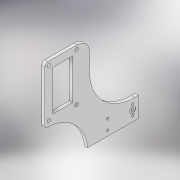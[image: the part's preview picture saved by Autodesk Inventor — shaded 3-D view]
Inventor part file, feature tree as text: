
AUTODESK INVENTOR PART (.ipt)
format: ipt  version: 2019 (Build 230136000, 136)  size: 181,248 bytes
history: native  units: mm
features: sketch x5, hole x4, extrude x1, other x1
ambient origin geometry x8: Origin, YZ Plane, XZ Plane, XY Plane, X Axis, Y Axis, Z Axis, Center Point
bodies: Solid1 (feature_tree)
feature tree (11):
  hole  "Hole1"  [1 undecoded]
  hole  "Hole2"  [1 undecoded]
  hole  "Hole3"  [1 undecoded]
  extrude  "Extrusion1"  [1 undecoded]
  hole  "Hole4"  [1 undecoded]
  sketch  "Sketch1"  dims[d0=6.756mm d1=6.0mm d2=12.878mm d3=2.0mm d4=14.3mm d5=78.0mm d6=20.594885mm]
  sketch  "Sketch2"  dims[d7=4.496mm d8=6.0mm d9=8.433mm d10=2.0mm d11=14.3mm d12=78.0mm d13=20.594885mm]
  sketch  "Sketch3"  dims[d14=4.496mm d15=6.0mm d16=8.433mm d17=2.0mm d18=14.3mm d19=78.0mm d20=20.594885mm d21=5.0mm]
  sketch  "Sketch4"  dims[d22=6.0mm d23=0.0mm]
  sketch  "Sketch5"  dims[d24=5.105mm d25=6.0mm d26=9.779mm d27=2.0mm d28=14.3mm d29=78.0mm d30=20.594885mm]
  other  "plate (2)"
note: 5 required parameter values undecoded (feature->parameter linkage not recoverable at this tier; creation-order binding heuristic only, values carry confidence <= 0.55)
